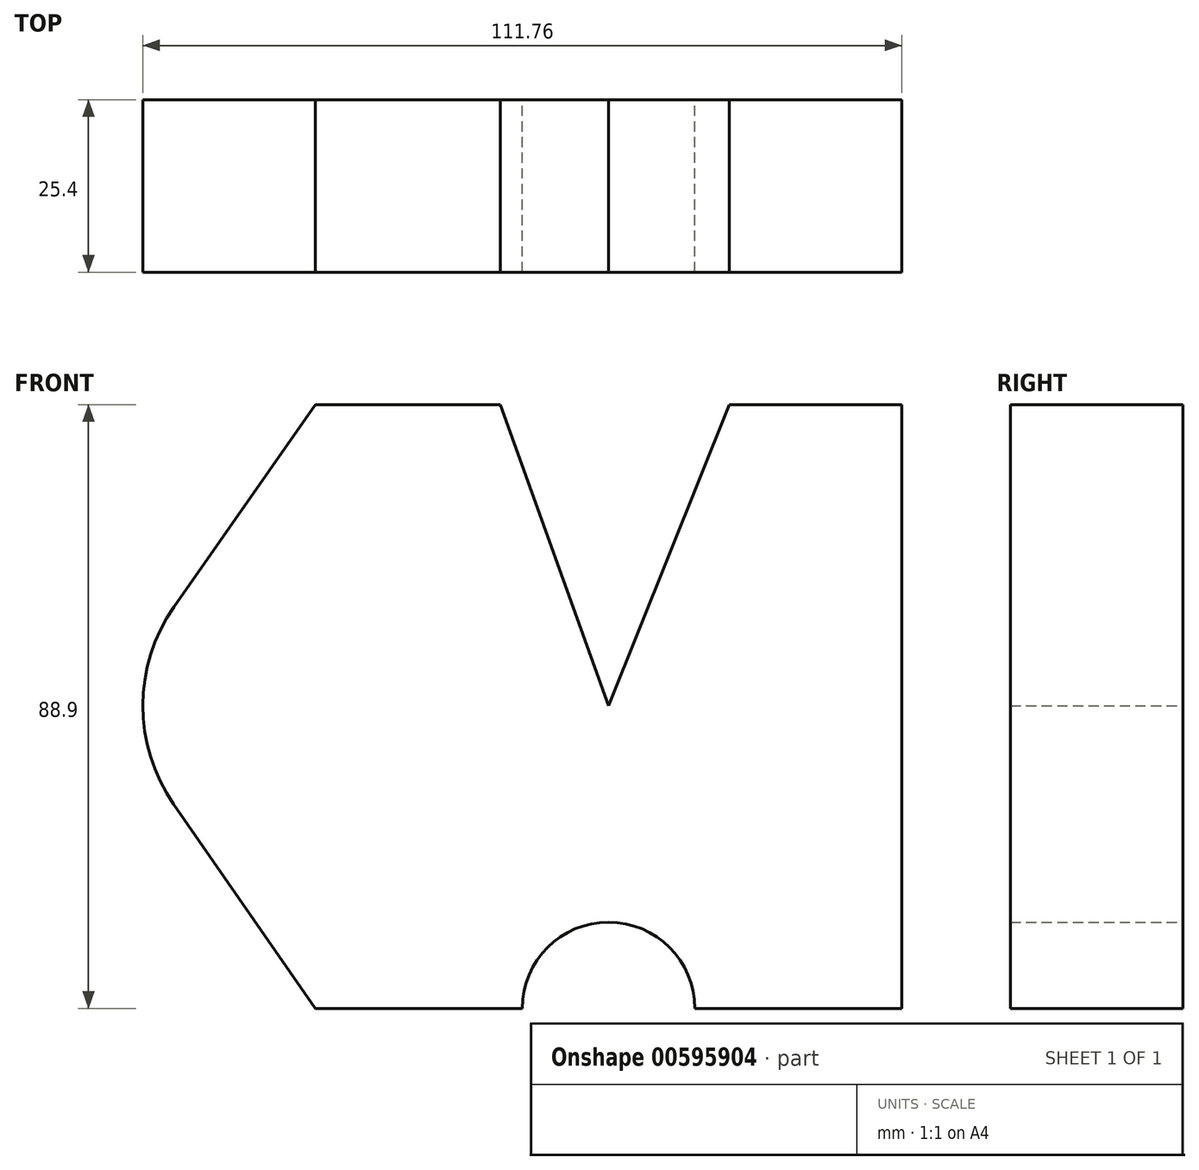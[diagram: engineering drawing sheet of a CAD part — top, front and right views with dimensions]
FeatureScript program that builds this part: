
annotation { "Feature Type Name" : "Feature", "Feature Type Description" : "" }
export const myFeature = defineFeature(function(context is Context, id is Id, definition is map)
    precondition{}
    {
        {
            var Q0;
            Q0=qCreatedBy(makeId("Front.planeOp"),FACE);
            var sketch = newSketch(context, id + "F0", { "sketchPlane" : qUnion([Q0])});
            skLineSegment(sketch, "E0", {"start": v(0, 0) * mm, "end": v(17.78, 44.34) * mm});
            skLineSegment(sketch, "E1", {"start": v(17.78, 44.34) * mm, "end": v(43.18, 44.34) * mm});
            skLineSegment(sketch, "E2", {"start": v(43.18, 44.34) * mm, "end": v(43.18, -44.56) * mm});
            skLineSegment(sketch, "E3", {"start": v(43.18, -44.56) * mm, "end": v(12.7, -44.56) * mm});
            skArc(sketch, "E4", {"start": v(12.7, -44.56) * mm, "mid": v(0, -31.86) * mm, "end": v(-12.7, -44.56) * mm});
            skLineSegment(sketch, "E5", {"start": v(-12.7, -44.56) * mm, "end": v(-43.18, -44.56) * mm});
            skLineSegment(sketch, "E6", {"start": v(-43.18, -44.56) * mm, "end": v(-64.05, -14.48) * mm});
            skArc(sketch, "E7", {"start": v(-64, 14.55) * mm, "mid": v(-68.58, 0.04) * mm, "end": v(-64.05, -14.48) * mm});
            skLineSegment(sketch, "E8", {"start": v(-64, 14.55) * mm, "end": v(-43.18, 44.34) * mm});
            skLineSegment(sketch, "E9", {"start": v(-15.92, 44.34) * mm, "end": v(0, 0) * mm});
            skLineSegment(sketch, "E10", {"start": v(-43.18, 44.34) * mm, "end": v(-43.18, -44.56) * mm, "construction": true});
            skLineSegment(sketch, "E11", {"start": v(-43.18, 44.34) * mm, "end": v(-15.92, 44.34) * mm});
            skSolve(sketch);
        }
        {
            var Q0;
            Q0 = qSketchRegion(id + "F0", true);
            extrude(context, id + "F1", {"entities" : qUnion([Q0]), "depth" : 25.4 * mm, "offsetDistance" : 25.4 * mm});
        }
    });
